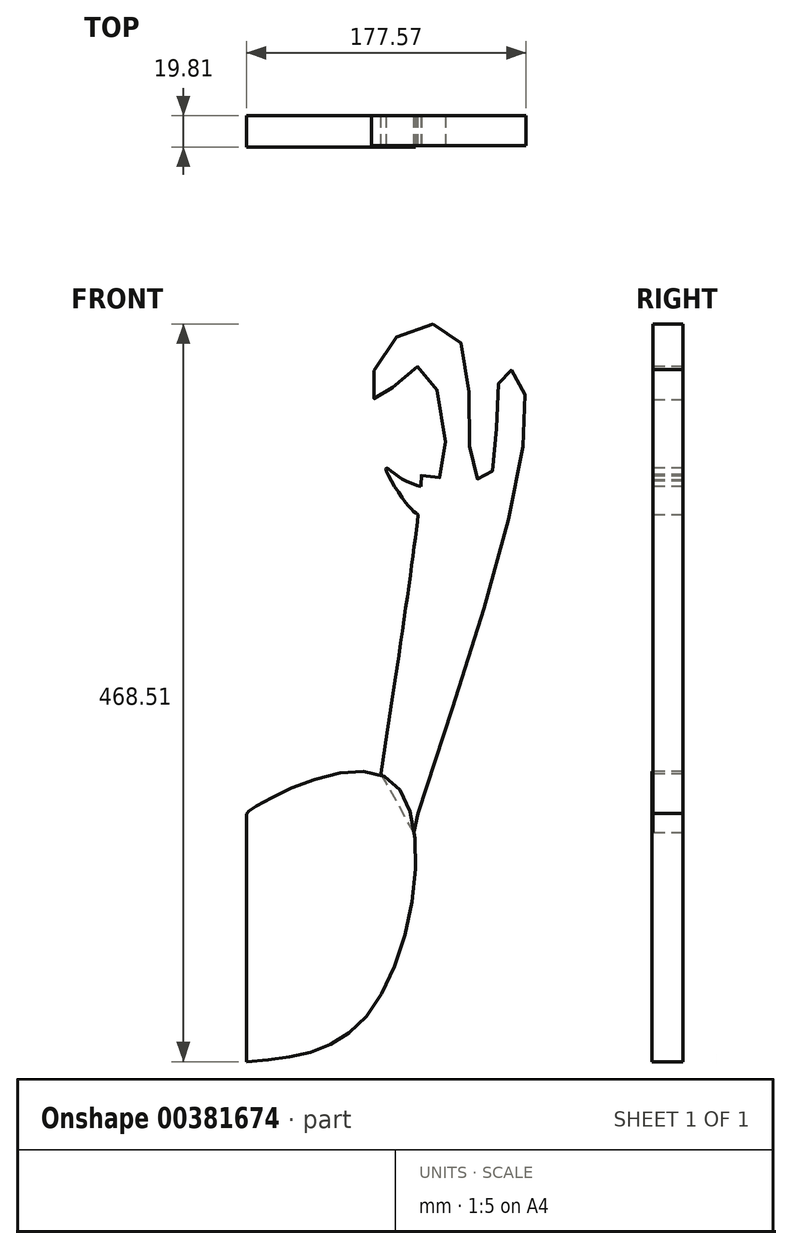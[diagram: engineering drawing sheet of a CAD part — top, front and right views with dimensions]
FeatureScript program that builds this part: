
annotation { "Feature Type Name" : "Feature", "Feature Type Description" : "" }
export const myFeature = defineFeature(function(context is Context, id is Id, definition is map)
    precondition{}
    {
        {
            var Q0;
            Q0=qCreatedBy(makeId("Front.planeOp"),FACE);
            var sketch = newSketch(context, id + "F0", { "sketchPlane" : qUnion([Q0])});
            skFitSpline(sketch, "E0", {"points": [v(0, 76.51) * mm, v(4.9, 80.65) * mm, v(89.72, 99.16) * mm, v(81.25, -45.27) * mm, v(0, -80.76) * mm], "startDerivative": vector(29.31, 37.8) * mm, "endDerivative": vector(-319.58, -24.73) * mm});
            skLineSegment(sketch, "E1", {"start": v(0, 76.51) * mm, "end": v(0, -80.76) * mm});
            skFitSpline(sketch, "E2.0", {"points": [v(4.22, 73.25) * mm, v(4.3, 73.34) * mm, v(4.42, 73.5) * mm, v(4.56, 73.68) * mm, v(4.68, 73.81) * mm, v(4.87, 74.02) * mm, v(5.29, 74.4) * mm, v(6.3, 75.17) * mm, v(7.94, 76.28) * mm, v(10.33, 77.76) * mm, v(13.35, 79.5) * mm, v(16.9, 81.45) * mm, v(20.95, 83.53) * mm, v(26.87, 86.4) * mm, v(35.11, 90.01) * mm, v(45.8, 93.92) * mm, v(56.72, 96.91) * mm, v(65.51, 98.27) * mm, v(72.04, 98.49) * mm, v(76.6, 98.18) * mm, v(80.05, 97.52) * mm, v(82.58, 96.74) * mm, v(84.35, 96.03) * mm, v(86.01, 95.2) * mm, v(87.55, 94.23) * mm, v(89.01, 93.11) * mm, v(90.87, 91.41) * mm, v(93.03, 88.87) * mm, v(95.34, 85.16) * mm, v(97.34, 80.81) * mm, v(99.58, 74.23) * mm, v(101.52, 64.7) * mm, v(102.43, 51.66) * mm, v(102, 37.55) * mm, v(100.3, 22.84) * mm, v(97.42, 8.02) * mm, v(93.49, -6.46) * mm, v(89.42, -17.85) * mm, v(85.77, -26.32) * mm, v(82.85, -32.29) * mm, v(80.27, -36.9) * mm, v(78.15, -40.33) * mm, v(75.98, -43.58) * mm, v(73.19, -47.32) * mm, v(69.71, -51.33) * mm, v(66.12, -54.89) * mm, v(61.17, -59.08) * mm, v(54.7, -63.4) * mm, v(46.47, -67.32) * mm, v(37.8, -70.21) * mm, v(28.7, -72.27) * mm, v(16.1, -74.16) * mm, v(6.25, -74.93) * mm, v(-0.41, -75.44) * mm]});
            skLineSegment(sketch, "E2.1", {"start": v(5.33, 74.42) * mm, "end": v(5.33, -75) * mm});
            skSolve(sketch);
        }
        {
            var Q0;
            Q0=makeQuery(id+"F0.imprint","IMPRINT",FACE,{"disambiguationData":[TD([[makeQuery(id+"F0.imprint","IMPRINT",EDGE,{"derivedFrom":sQuery(id+"F0.wireOp",EDGE,"E0")}),-1.0]])]});
            extrude(context, id + "F1", {"entities" : qUnion([Q0]), "depth" : 19.8 * mm});
        }
        {
            var Q0;
            Q0=qCreatedBy(makeId("Front.planeOp"),FACE);
            var sketch = newSketch(context, id + "F2", { "sketchPlane" : qUnion([Q0])});
            skFitSpline(sketch, "E3", {"points": [v(84.2, 93.59) * mm, v(109.07, 266.75) * mm, v(111.83, 300.83) * mm], "startDerivative": vector(45.17, 297.76) * mm, "endDerivative": vector(4.9, 89.93) * mm});
            skFitSpline(sketch, "E4", {"points": [v(111.33, 291.64) * mm, v(123.8, 291.64) * mm, v(111.33, 360.7) * mm, v(83.28, 339.52) * mm, v(86.96, 370.84) * mm, v(133.02, 380.97) * mm, v(145, 291.64) * mm, v(155.12, 291.64) * mm, v(162.5, 357.02) * mm, v(174.47, 351.5) * mm, v(109.07, 77) * mm], "startDerivative": vector(296.88, -151.26) * mm, "endDerivative": vector(-511.52, -1548.77) * mm});
            skLineSegment(sketch, "E5", {"start": v(109.07, 77) * mm, "end": v(106.41, 64.75) * mm});
            skFitSpline(sketch, "E6", {"points": [v(109.07, 266.75) * mm, v(101.1, 274.45) * mm, v(88.68, 296.1) * mm, v(96.97, 290.7) * mm, v(110.8, 284.5) * mm], "startDerivative": vector(-31.07, 22) * mm, "endDerivative": vector(53.47, -17.6) * mm});
            skLineSegment(sketch, "E7", {"start": v(106.41, 64.75) * mm, "end": v(85.53, 102.32) * mm});
            skLineSegment(sketch, "E8", {"start": v(111.33, 291.64) * mm, "end": v(111.33, 292.13) * mm});
            skSolve(sketch);
        }
        {
            var Q0;
            Q0=makeQuery(id+"F2.imprint","IMPRINT",FACE,{"disambiguationData":[TD([[makeQuery(id+"F2.imprint","IMPRINT",EDGE,{"derivedFrom":sQuery(id+"F2.wireOp",EDGE,"E4")}),-1.0]])]});
            var Q1;
            {var subQ0=sQuery(id+"F2.wireOp",EDGE,"E6");Q1=makeQuery(id+"F2.imprint","IMPRINT",FACE,{"disambiguationData":[TD([[makeQuery(id+"F2.imprint","IMPRINT",EDGE,{"derivedFrom":subQ0}),-1.0]])]});}
            extrude(context, id + "F3", {"entities" : qUnion([Q0, Q1]), "depth" : 19.05 * mm});
        }
    });
